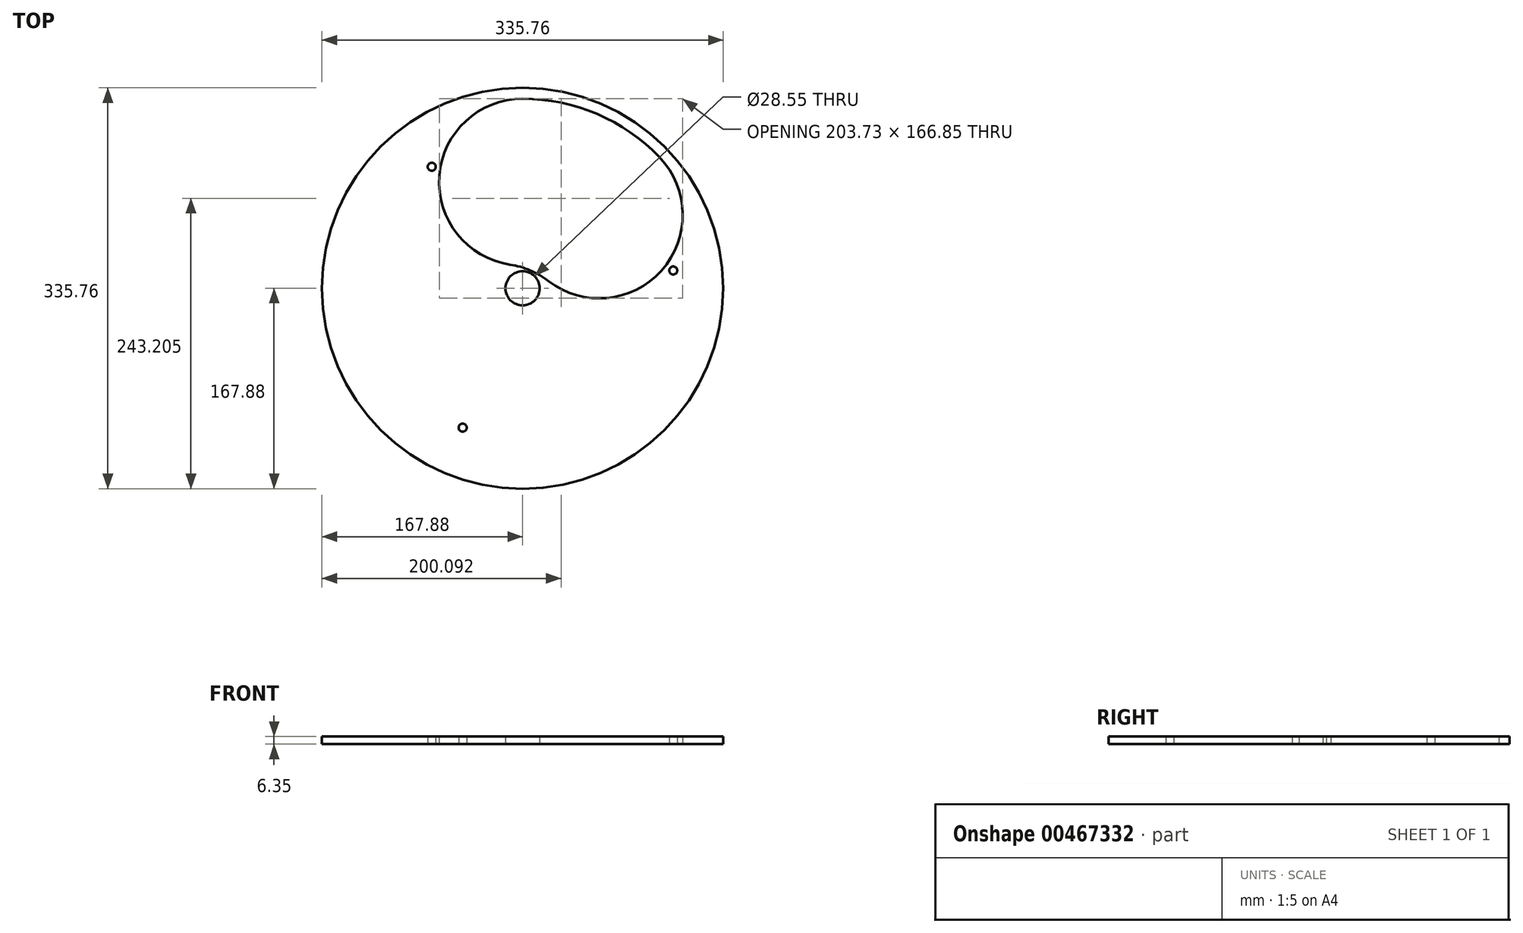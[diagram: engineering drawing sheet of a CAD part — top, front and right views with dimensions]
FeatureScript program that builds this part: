
annotation { "Feature Type Name" : "Feature", "Feature Type Description" : "" }
export const myFeature = defineFeature(function(context is Context, id is Id, definition is map)
    precondition{}
    {
        {
            var Q0;
            Q0=qCreatedBy(makeId("Top.planeOp"),FACE);
            var sketch = newSketch(context, id + "F0", { "sketchPlane" : qUnion([Q0])});
            skCircle(sketch, "E0", {"center": v(0, 0) * mm, "radius": 167.88 * mm});
            skCircle(sketch, "E1", {"center": v(0, 0) * mm, "radius": 88.9 * mm, "construction": true});
            skCircle(sketch, "E2", {"center": v(0, 88.9) * mm, "radius": 69.85 * mm});
            skCircle(sketch, "E3", {"center": v(64.23, 61.46) * mm, "radius": 69.85 * mm});
            skCircle(sketch, "E4", {"center": v(0, 0) * mm, "radius": 158.75 * mm});
            skCircle(sketch, "E5", {"center": v(-21.02, -49.2) * mm, "radius": 69.85 * mm});
            skCircle(sketch, "E6", {"center": v(0, 0) * mm, "radius": 14.27 * mm});
            skCircle(sketch, "E7", {"center": v(0, 0) * mm, "radius": 127 * mm, "construction": true});
            skCircle(sketch, "E8", {"center": v(-50.14, -116.68) * mm, "radius": 3.37 * mm});
            skCircle(sketch, "E9.1.0", {"center": v(126.12, 14.92) * mm, "radius": 3.37 * mm});
            skCircle(sketch, "E9.2.0", {"center": v(-75.98, 101.76) * mm, "radius": 3.37 * mm});
            skSolve(sketch);
        }
        {
            var Q0;
            Q0=makeQuery(id+"F0.imprint","IMPRINT",FACE,{"disambiguationData":[TD([[makeQuery(id+"F0.imprint","IMPRINT",EDGE,{"derivedFrom":sQuery(id+"F0.wireOp",EDGE,"E0")}),1.0]])]});
            var Q1;
            Q1=makeQuery(id+"F0.imprint","IMPRINT",FACE,{"disambiguationData":[TD([[makeQuery(id+"F0.imprint","IMPRINT",EDGE,{"derivedFrom":sQuery(id+"F0.wireOp",EDGE,"E8")}),-1.0]])]});
            var Q2;
            Q2=makeQuery(id+"F0.imprint","IMPRINT",FACE,{"disambiguationData":[TD([[makeQuery(id+"F0.imprint","IMPRINT",EDGE,{"derivedFrom":sQuery(id+"F0.wireOp",EDGE,"E6")}),-1.0]])]});
            extrude(context, id + "F1", {"entities" : qUnion([Q0, Q1, Q2]), "depth" : 6.35 * mm});
        }
    });
